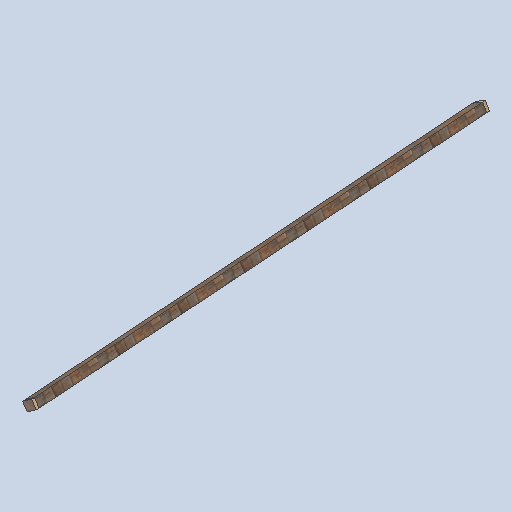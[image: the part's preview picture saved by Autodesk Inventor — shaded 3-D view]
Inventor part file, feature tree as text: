
AUTODESK INVENTOR PART (.ipt)
format: ipt  version: 2024.2 (Build 282272000, 272)  size: 135,680 bytes
history: native  units: in
note: dims shown in document units (in); Inventor stores cm internally (conversion verified against a paired STEP export)
features: sketch x4, other x3, plane x2
ambient origin geometry x8: Origin, YZ Plane, XZ Plane, XY Plane, X Axis, Y Axis, Z Axis, Center Point
bodies: Solid1 (feature_tree)
feature tree (9):
  other  "support_beam_segment_0103.ipt"
  other  "Solid1::support_beam_segment_0103.ipt"
  other  "TaggingFeature1"
  sketch  "Sketch1"  dims[d0=0.3937in]
  sketch  "Sketch2"
  sketch  "Sketch3"
  sketch  "Sketch4"
  plane  "Work Plane1"
  plane  "Work Plane2"
